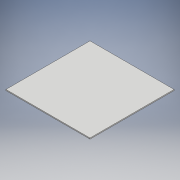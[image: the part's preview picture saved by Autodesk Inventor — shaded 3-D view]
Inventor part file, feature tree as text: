
AUTODESK INVENTOR PART (.ipt)
format: ipt  version: 2017 (Build 210142000, 142)  size: 88,576 bytes
history: native  units: mm
features: extrude x1, sketch x1
ambient origin geometry x8: Origin, YZ Plane, XZ Plane, XY Plane, X Axis, Y Axis, Z Axis, Center Point
bodies: Solid1 (feature_tree)
feature tree (2):
  extrude  "Extrusion1"  Depth=244.0mm
  sketch  "Sketch1"  dims[d0=244.0mm d1=244.0mm d2=3.0mm d3=0.0mm]
